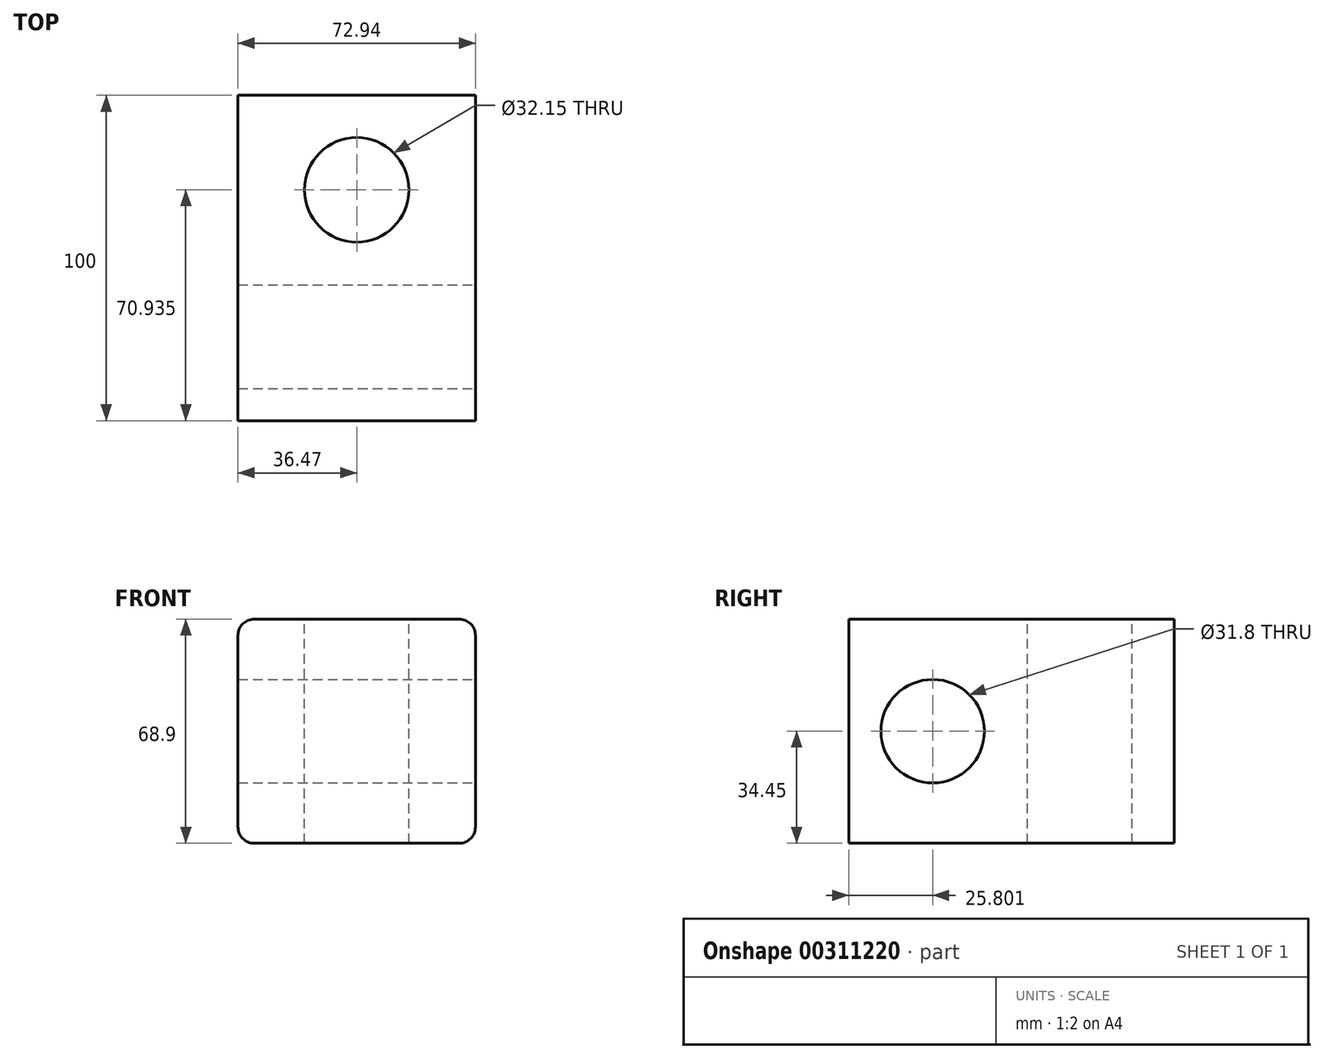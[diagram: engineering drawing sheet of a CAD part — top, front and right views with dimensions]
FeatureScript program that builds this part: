
annotation { "Feature Type Name" : "Feature", "Feature Type Description" : "" }
export const myFeature = defineFeature(function(context is Context, id is Id, definition is map)
    precondition{}
    {
        {
            var Q0;
            Q0=qCreatedBy(makeId("Front.planeOp"),FACE);
            var sketch = newSketch(context, id + "F0", { "sketchPlane" : qUnion([Q0])});
            skLineSegment(sketch, "E0.bottom", {"start": v(-36.47, 34.45) * mm, "end": v(36.47, 34.45) * mm});
            skLineSegment(sketch, "E0.top", {"start": v(-36.47, -34.45) * mm, "end": v(36.47, -34.45) * mm});
            skLineSegment(sketch, "E0.left", {"start": v(-36.47, 34.45) * mm, "end": v(-36.47, -34.45) * mm});
            skLineSegment(sketch, "E0.right", {"start": v(36.47, 34.45) * mm, "end": v(36.47, -34.45) * mm});
            skPoint(sketch, "E0.middle", {"position": v(0, 0) * mm});
            skSolve(sketch);
        }
        {
            var Q0;
            Q0 = qSketchRegion(id + "F0", true);
            extrude(context, id + "F1", {"entities" : qUnion([Q0]), "endBound" : BoundingType.SYMMETRIC, "depth" : 100 * mm});
        }
        {
            var Q0;
            Q0=makeQuery(id+"F1.opExtrude","SWEPT_FACE",FACE,{"disambiguationData":[OSD([sQuery(id+"F0.wireOp",EDGE,"E0.right")])]});
            var sketch = newSketch(context, id + "F2", { "sketchPlane" : qUnion([Q0])});
            skCircle(sketch, "E1", {"center": v(-24.2, 0) * mm, "radius": 21.1 * mm});
            skSolve(sketch);
        }
        {
            var Q0;
            Q0=makeQuery(id+"F1.opExtrude","SWEPT_EDGE",EDGE,{"disambiguationData":[OSD([sQuery(id+"F0.wireOp",EDGE,"E0.bottom"),sQuery(id+"F0.wireOp",EDGE,"E0.right")])]});
            var Q1;
            Q1=makeQuery(id+"F1.opExtrude","SWEPT_EDGE",EDGE,{"disambiguationData":[OSD([sQuery(id+"F0.wireOp",EDGE,"E0.bottom"),sQuery(id+"F0.wireOp",EDGE,"E0.left")])]});
            var Q2;
            Q2=makeQuery(id+"F1.opExtrude","SWEPT_EDGE",EDGE,{"disambiguationData":[OSD([sQuery(id+"F0.wireOp",EDGE,"E0.top"),sQuery(id+"F0.wireOp",EDGE,"E0.right")])]});
            var Q3;
            Q3=makeQuery(id+"F1.opExtrude","SWEPT_EDGE",EDGE,{"disambiguationData":[OSD([sQuery(id+"F0.wireOp",EDGE,"E0.top"),sQuery(id+"F0.wireOp",EDGE,"E0.left")])]});
            fillet(context, id + "F3", {"entities" : qUnion([Q0, Q1, Q2, Q3]), "radius" : 5 * mm, "tangentPropagation" : true, "allowEdgeOverflow" : false});
        }
        {
            var Q0;
            Q0=sQuery(id+"F2.wireOp",VERTEX,"E1.center");
            var Q1;
            Q1=makeQuery(id+"F1.opExtrude","SWEPT_BODY",BODY,{"disambiguationData":[OSD([sQuery(id+"F0.wireOp",EDGE,"E0.bottom"),sQuery(id+"F0.wireOp",EDGE,"E0.top"),sQuery(id+"F0.wireOp",EDGE,"E0.left"),sQuery(id+"F0.wireOp",EDGE,"E0.right")])]});
            hole(context, id + "F4", {"style" : HoleStyle.SIMPLE, "endStyle" : HoleEndStyle.THROUGH, "holeDiameter" : 31.8 * mm, "tappedDepth" : 12.7 * mm, "tapClearance" : 3, "locations" : qUnion([Q0]), "scope" : qUnion([Q1])});
        }
        {
            var Q0;
            Q0=makeQuery(id+"F1.opExtrude","SWEPT_FACE",FACE,{"disambiguationData":[OSD([sQuery(id+"F0.wireOp",EDGE,"E0.bottom")])]});
            var sketch = newSketch(context, id + "F5", { "sketchPlane" : qUnion([Q0])});
            skCircle(sketch, "E2", {"center": v(0, 20.93) * mm, "radius": 25.27 * mm});
            skSolve(sketch);
        }
        {
            var Q0;
            Q0=sQuery(id+"F5.wireOp",VERTEX,"E2.center");
            var Q1;
            Q1=makeQuery(id+"F1.opExtrude","SWEPT_BODY",BODY,{"disambiguationData":[OSD([sQuery(id+"F0.wireOp",EDGE,"E0.bottom"),sQuery(id+"F0.wireOp",EDGE,"E0.top"),sQuery(id+"F0.wireOp",EDGE,"E0.left"),sQuery(id+"F0.wireOp",EDGE,"E0.right")])]});
            hole(context, id + "F6", {"style" : HoleStyle.SIMPLE, "endStyle" : HoleEndStyle.THROUGH, "standardTappedOrClearance" : lookupTablePath({ "standard" : "ANSI", "fit" : "Close", "size" : "1 1/4", "type" : "Clearance" }), "standardBlindInLast" : lookupTablePath({ "fit" : "Close", "standard" : "ANSI", "size" : "1 1/4", "type" : "Clearance" }), "holeDiameter" : 32.15 * mm, "tappedDepth" : 12.7 * mm, "tapClearance" : 3, "locations" : qUnion([Q0]), "scope" : qUnion([Q1])});
        }
    });
